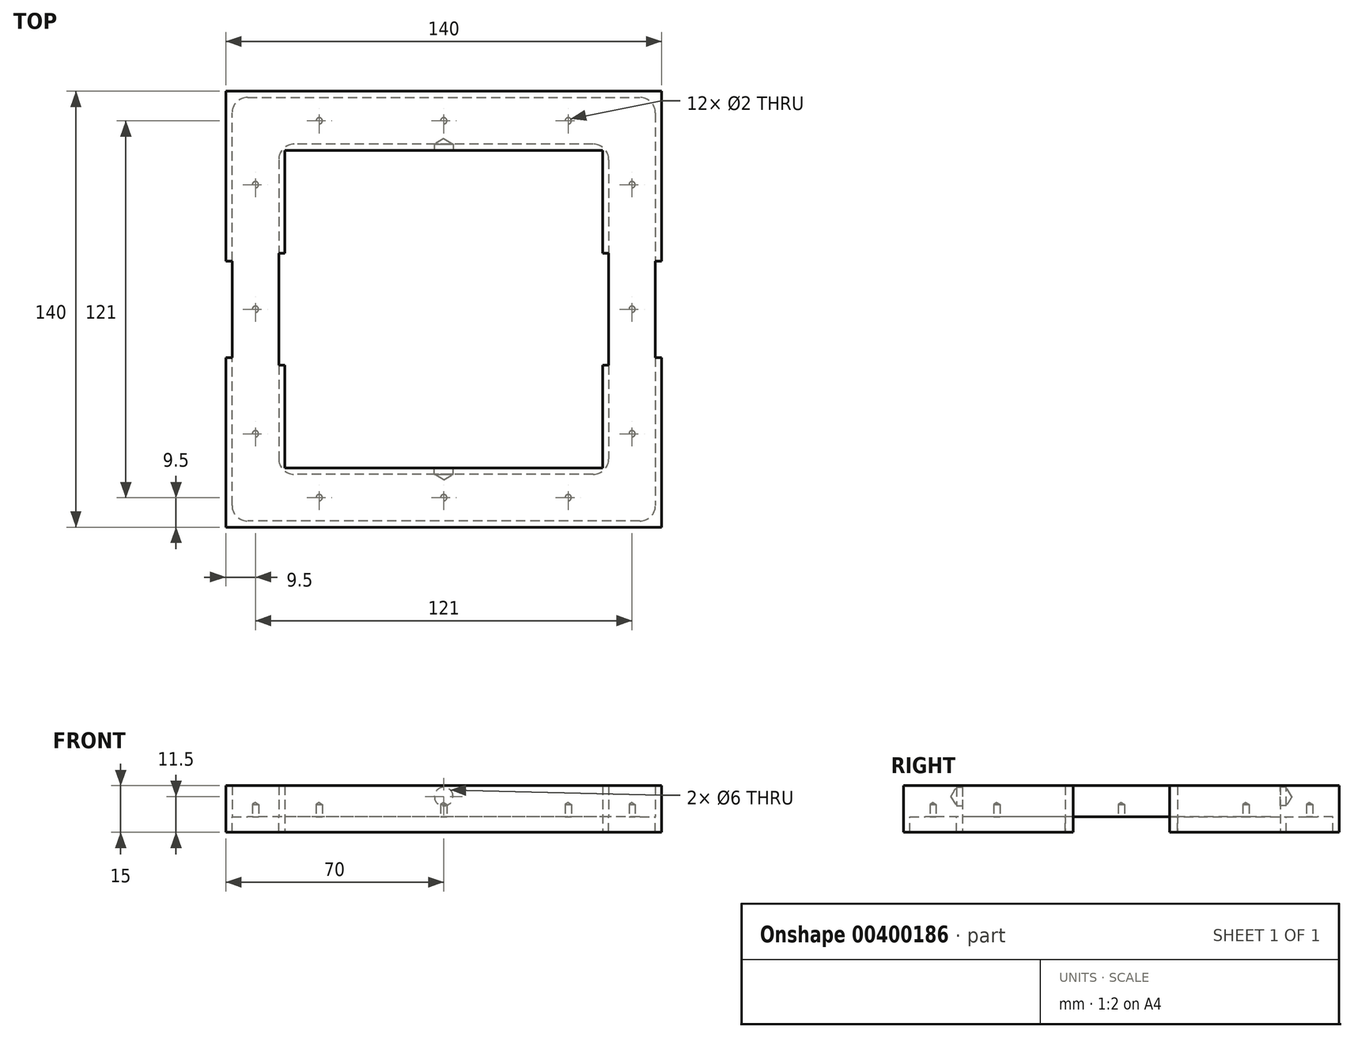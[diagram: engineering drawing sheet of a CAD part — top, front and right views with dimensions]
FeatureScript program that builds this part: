
annotation { "Feature Type Name" : "Feature", "Feature Type Description" : "" }
export const myFeature = defineFeature(function(context is Context, id is Id, definition is map)
    precondition{}
    {
        {
            var Q0;
            Q0=qCreatedBy(makeId("Top.planeOp"),FACE);
            var sketch = newSketch(context, id + "F0", { "sketchPlane" : qUnion([Q0])});
            skLineSegment(sketch, "E0.bottom", {"start": v(-70, 70) * mm, "end": v(70, 70) * mm});
            skLineSegment(sketch, "E0.top", {"start": v(-70, -70) * mm, "end": v(70, -70) * mm});
            skLineSegment(sketch, "E0.left", {"start": v(-70, 70) * mm, "end": v(-70, -70) * mm});
            skLineSegment(sketch, "E0.right", {"start": v(70, 70) * mm, "end": v(70, -70) * mm});
            skPoint(sketch, "E0.middle", {"position": v(0, 0) * mm});
            skLineSegment(sketch, "E1", {"start": v(68, 68) * mm, "end": v(68, -68) * mm});
            skLineSegment(sketch, "E2", {"start": v(68, -68) * mm, "end": v(-68, -68) * mm});
            skLineSegment(sketch, "E3", {"start": v(-68, -68) * mm, "end": v(-68, 68) * mm});
            skLineSegment(sketch, "E4", {"start": v(-68, 68) * mm, "end": v(68, 68) * mm});
            skLineSegment(sketch, "E5", {"start": v(53, -53) * mm, "end": v(-53, -53) * mm});
            skLineSegment(sketch, "E6", {"start": v(51, -51) * mm, "end": v(-51, -51) * mm});
            skLineSegment(sketch, "E7", {"start": v(-51, 51) * mm, "end": v(51, 51) * mm});
            skLineSegment(sketch, "E8", {"start": v(53, 53) * mm, "end": v(-53, 53) * mm});
            skLineSegment(sketch, "E9", {"start": v(-53, 53) * mm, "end": v(-53, -53) * mm});
            skLineSegment(sketch, "E10", {"start": v(-51, 51) * mm, "end": v(-51, -51) * mm});
            skLineSegment(sketch, "E11", {"start": v(-51, 0) * mm, "end": v(-51, 18) * mm});
            skLineSegment(sketch, "E12", {"start": v(-51, 18) * mm, "end": v(-53, 18) * mm});
            skLineSegment(sketch, "E13", {"start": v(-53, 18) * mm, "end": v(-53, -18) * mm});
            skLineSegment(sketch, "E14", {"start": v(-53, -18) * mm, "end": v(-51, -18) * mm});
            skLineSegment(sketch, "E15", {"start": v(-51, -18) * mm, "end": v(-51, 0) * mm});
            skLineSegment(sketch, "E16", {"start": v(51, 51) * mm, "end": v(51, -51) * mm});
            skLineSegment(sketch, "E17", {"start": v(53, 53) * mm, "end": v(53, -53) * mm});
            skLineSegment(sketch, "E18", {"start": v(53, 0) * mm, "end": v(53, 18) * mm});
            skLineSegment(sketch, "E19", {"start": v(53, 18) * mm, "end": v(51, 18) * mm});
            skLineSegment(sketch, "E20", {"start": v(53, 0) * mm, "end": v(53, -18) * mm});
            skLineSegment(sketch, "E21", {"start": v(53, -18) * mm, "end": v(51, -18) * mm});
            skLineSegment(sketch, "E22", {"start": v(68, 0) * mm, "end": v(68, 15.5) * mm});
            skLineSegment(sketch, "E23", {"start": v(68, 15.5) * mm, "end": v(70, 15.5) * mm});
            skLineSegment(sketch, "E24", {"start": v(68, 0) * mm, "end": v(68, -15.5) * mm});
            skLineSegment(sketch, "E25", {"start": v(68, -15.5) * mm, "end": v(70, -15.5) * mm});
            skLineSegment(sketch, "E26", {"start": v(-68, 0) * mm, "end": v(-68, 15.5) * mm});
            skLineSegment(sketch, "E27", {"start": v(-68, 15.5) * mm, "end": v(-70, 15.5) * mm});
            skLineSegment(sketch, "E28", {"start": v(-68, 0) * mm, "end": v(-68, -15.5) * mm});
            skLineSegment(sketch, "E29", {"start": v(-68, -15.5) * mm, "end": v(-70, -15.5) * mm});
            skPoint(sketch, "E30", {"position": v(0, -60.5) * mm});
            skPoint(sketch, "E31", {"position": v(60.5, 0) * mm});
            skPoint(sketch, "E32", {"position": v(0, 60.5) * mm});
            skPoint(sketch, "E33", {"position": v(-60.5, 0) * mm});
            skPoint(sketch, "E34", {"position": v(-40, -60.5) * mm});
            skPoint(sketch, "E35", {"position": v(40, -60.5) * mm});
            skPoint(sketch, "E36", {"position": v(-40, 60.5) * mm});
            skPoint(sketch, "E37", {"position": v(40, 60.5) * mm});
            skPoint(sketch, "E38", {"position": v(-60.5, -40) * mm});
            skPoint(sketch, "E39", {"position": v(-60.5, 40) * mm});
            skPoint(sketch, "E40", {"position": v(60.5, -40) * mm});
            skPoint(sketch, "E41", {"position": v(60.5, 40) * mm});
            skSolve(sketch);
        }
        {
            var Q0;
            Q0=makeQuery(id+"F0.imprint","IMPRINT",FACE,{"disambiguationData":[TD([[makeQuery(id+"F0.imprint","IMPRINT",EDGE,{"derivedFrom":sQuery(id+"F0.wireOp",EDGE,"E0.bottom")}),-1.0]])]});
            var Q1;
            Q1=makeQuery(id+"F0.imprint","IMPRINT",FACE,{"disambiguationData":[TD([[makeQuery(id+"F0.imprint","IMPRINT",EDGE,{"derivedFrom":sQuery(id+"F0.wireOp",EDGE,"E1")}),-1.0]])]});
            var Q2;
            Q2=makeQuery(id+"F0.imprint","IMPRINT",FACE,{"disambiguationData":[TD([[makeQuery(id+"F0.imprint","IMPRINT",EDGE,{"derivedFrom":sQuery(id+"F0.wireOp",EDGE,"Wn8sRztM-9DSE-PQQb-c3jE-AxI3LFL1xT7E")}),-1.0]])]});
            var Q3;
            Q3=makeQuery(id+"F0.imprint","IMPRINT",FACE,{"disambiguationData":[TD([[makeQuery(id+"F0.imprint","IMPRINT",EDGE,{"derivedFrom":sQuery(id+"F0.wireOp",EDGE,"heY1r5AS-22mk-dWtd-xOAW-OfOOxzFGAM1P")}),-1.0]])]});
            var Q4;
            {var subQ4=sQuery(id+"F0.wireOp",EDGE,"0ZnLiHHq-RTrH-7G8n-jalu-C7bSdwdgHh1i");Q4=makeQuery(id+"F0.imprint","IMPRINT",FACE,{"disambiguationData":[TD([[makeQuery(id+"F0.imprint","IMPRINT",EDGE,{"derivedFrom":subQ4}),1.0]])]});}
            var Q5;
            Q5=makeQuery(id+"F0.imprint","IMPRINT",FACE,{"disambiguationData":[TD([[makeQuery(id+"F0.imprint","IMPRINT",EDGE,{"derivedFrom":sQuery(id+"F0.wireOp",EDGE,"E26")}),1.0]])]});
            var Q6;
            {var subQ1=sQuery(id+"F0.wireOp",EDGE,"E0.top");Q6=makeQuery(id+"F0.imprint","IMPRINT",FACE,{"disambiguationData":[TD([[makeQuery(id+"F0.imprint","IMPRINT",EDGE,{"derivedFrom":subQ1}),1.0]])]});}
            var Q7;
            Q7=makeQuery(id+"F0.imprint","IMPRINT",FACE,{"disambiguationData":[TD([[makeQuery(id+"F0.imprint","IMPRINT",EDGE,{"derivedFrom":sQuery(id+"F0.wireOp",EDGE,"E22")}),-1.0]])]});
            var Q8;
            {var subQ1=sQuery(id+"F0.wireOp",EDGE,"E7");Q8=makeQuery(id+"F0.imprint","IMPRINT",FACE,{"disambiguationData":[TD([[makeQuery(id+"F0.imprint","IMPRINT",EDGE,{"derivedFrom":subQ1}),1.0]])]});}
            var Q9;
            Q9=makeQuery(id+"F0.imprint","IMPRINT",FACE,{"disambiguationData":[TD([[makeQuery(id+"F0.imprint","IMPRINT",EDGE,{"derivedFrom":sQuery(id+"F0.wireOp",EDGE,"E11")}),1.0]])]});
            var Q10;
            Q10=makeQuery(id+"F0.imprint","IMPRINT",FACE,{"disambiguationData":[TD([[makeQuery(id+"F0.imprint","IMPRINT",EDGE,{"derivedFrom":sQuery(id+"F0.wireOp",EDGE,"E18")}),1.0]])]});
            var Q11;
            {var subQ4=sQuery(id+"F0.wireOp",EDGE,"E5");Q11=makeQuery(id+"F0.imprint","IMPRINT",FACE,{"disambiguationData":[TD([[makeQuery(id+"F0.imprint","IMPRINT",EDGE,{"derivedFrom":subQ4}),-1.0]])]});}
            extrude(context, id + "F1", {"entities" : qUnion([Q0, Q1, Q2, Q3, Q4, Q5, Q6, Q7, Q8, Q9, Q10, Q11]), "depth" : 10 * mm});
        }
        {
            var Q0;
            Q0=makeQuery(id+"F0.imprint","IMPRINT",FACE,{"disambiguationData":[TD([[makeQuery(id+"F0.imprint","IMPRINT",EDGE,{"derivedFrom":sQuery(id+"F0.wireOp",EDGE,"E0.bottom")}),-1.0]])]});
            var Q1;
            Q1=makeQuery(id+"F0.imprint","IMPRINT",FACE,{"disambiguationData":[TD([[makeQuery(id+"F0.imprint","IMPRINT",EDGE,{"derivedFrom":sQuery(id+"F0.wireOp",EDGE,"Wn8sRztM-9DSE-PQQb-c3jE-AxI3LFL1xT7E")}),-1.0]])]});
            var Q2;
            {var subQ1=sQuery(id+"F0.wireOp",EDGE,"E0.top");Q2=makeQuery(id+"F0.imprint","IMPRINT",FACE,{"disambiguationData":[TD([[makeQuery(id+"F0.imprint","IMPRINT",EDGE,{"derivedFrom":subQ1}),1.0]])]});}
            var Q3;
            {var subQ4=sQuery(id+"F0.wireOp",EDGE,"E5");Q3=makeQuery(id+"F0.imprint","IMPRINT",FACE,{"disambiguationData":[TD([[makeQuery(id+"F0.imprint","IMPRINT",EDGE,{"derivedFrom":subQ4}),-1.0]])]});}
            var Q4;
            {var subQ1=sQuery(id+"F0.wireOp",EDGE,"E7");Q4=makeQuery(id+"F0.imprint","IMPRINT",FACE,{"disambiguationData":[TD([[makeQuery(id+"F0.imprint","IMPRINT",EDGE,{"derivedFrom":subQ1}),1.0]])]});}
            extrude(context, id + "F2", {"entities" : qUnion([Q0, Q1, Q2, Q3, Q4]), "operationType" : NewBodyOperationType.ADD, "oppositeDirection" : true, "depth" : 5 * mm});
        }
        {
            var Q0;
            Q0=sQuery(id+"F0.wireOp",VERTEX,"6b741a85-5c8c-4f44-8248-58c756bbbfca");
            var Q1;
            Q1=sQuery(id+"F0.wireOp",VERTEX,"E30");
            var Q2;
            Q2=sQuery(id+"F0.wireOp",VERTEX,"30763c46-4e67-4485-9359-a76c1e7a9025");
            var Q3;
            Q3=sQuery(id+"F0.wireOp",VERTEX,"6d4f6b0a-0079-43d5-8c28-538648c8d0f5");
            var Q4;
            Q4=sQuery(id+"F0.wireOp",VERTEX,"E31");
            var Q5;
            Q5=sQuery(id+"F0.wireOp",VERTEX,"4c6b8f36-78a3-45b5-8b2e-6f7322aba786");
            var Q6;
            Q6=sQuery(id+"F0.wireOp",VERTEX,"8713927f-972c-453f-9c66-a7a60fbf4d67");
            var Q7;
            Q7=sQuery(id+"F0.wireOp",VERTEX,"E32");
            var Q8;
            Q8=sQuery(id+"F0.wireOp",VERTEX,"1defa935-9a37-4483-8ab3-138fc0cdace9");
            var Q9;
            Q9=sQuery(id+"F0.wireOp",VERTEX,"1ced1939-7057-40a5-9a17-9a71a5e9f090");
            var Q10;
            Q10=sQuery(id+"F0.wireOp",VERTEX,"E33");
            var Q11;
            Q11=sQuery(id+"F0.wireOp",VERTEX,"de10a42f-2d62-4ead-983f-996f2c1775ed");
            var Q12;
            Q12=sQuery(id+"F0.wireOp",VERTEX,"E38");
            var Q13;
            Q13=sQuery(id+"F0.wireOp",VERTEX,"E34");
            var Q14;
            Q14=sQuery(id+"F0.wireOp",VERTEX,"E35");
            var Q15;
            Q15=sQuery(id+"F0.wireOp",VERTEX,"E40");
            var Q16;
            Q16=sQuery(id+"F0.wireOp",VERTEX,"E41");
            var Q17;
            Q17=sQuery(id+"F0.wireOp",VERTEX,"E37");
            var Q18;
            Q18=sQuery(id+"F0.wireOp",VERTEX,"E36");
            var Q19;
            Q19=sQuery(id+"F0.wireOp",VERTEX,"E39");
            var Q20;
            Q20=makeQuery(id+"F1.opExtrude","SWEPT_BODY",BODY,{"disambiguationData":[OSD([sQuery(id+"F0.wireOp",EDGE,"E0.bottom"),sQuery(id+"F0.wireOp",EDGE,"E0.top"),sQuery(id+"F0.wireOp",EDGE,"E0.left"),sQuery(id+"F0.wireOp",EDGE,"E0.right"),sQuery(id+"F0.wireOp",EDGE,"E6"),sQuery(id+"F0.wireOp",EDGE,"E7"),sQuery(id+"F0.wireOp",EDGE,"E10"),sQuery(id+"F0.wireOp",EDGE,"E11"),sQuery(id+"F0.wireOp",EDGE,"E15"),sQuery(id+"F0.wireOp",EDGE,"E16")])]});
            hole(context, id + "F3", {"style" : HoleStyle.SIMPLE, "endStyle" : HoleEndStyle.BLIND, "oppositeDirection" : true, "holeDiameter" : 2 * mm, "holeDepth" : 4 * mm, "isTappedThrough" : true, "tappedDepth" : 12 * mm, "tapClearance" : 3, "locations" : qUnion([Q0, Q1, Q2, Q3, Q4, Q5, Q6, Q7, Q8, Q9, Q10, Q11, Q12, Q13, Q14, Q15, Q16, Q17, Q18, Q19]), "scope" : qUnion([Q20])});
        }
        {
            var Q0;
            Q0=makeQuery(id+"F2.opExtrude","SWEPT_EDGE",EDGE,{"disambiguationData":[OSD([sQuery(id+"F0.wireOp",EDGE,"E2"),sQuery(id+"F0.wireOp",EDGE,"E3")])]});
            var Q1;
            Q1=makeQuery(id+"F2.opExtrude","SWEPT_EDGE",EDGE,{"disambiguationData":[OSD([sQuery(id+"F0.wireOp",EDGE,"E5"),sQuery(id+"F0.wireOp",EDGE,"E9")])]});
            var Q2;
            Q2=makeQuery(id+"F2.opExtrude","SWEPT_EDGE",EDGE,{"disambiguationData":[OSD([sQuery(id+"F0.wireOp",EDGE,"E8"),sQuery(id+"F0.wireOp",EDGE,"E9")])]});
            var Q3;
            Q3=makeQuery(id+"F2.opExtrude","SWEPT_EDGE",EDGE,{"disambiguationData":[OSD([sQuery(id+"F0.wireOp",EDGE,"E8"),sQuery(id+"F0.wireOp",EDGE,"E17")])]});
            var Q4;
            Q4=makeQuery(id+"F2.opExtrude","SWEPT_EDGE",EDGE,{"disambiguationData":[OSD([sQuery(id+"F0.wireOp",EDGE,"E5"),sQuery(id+"F0.wireOp",EDGE,"E17")])]});
            var Q5;
            Q5=makeQuery(id+"F2.opExtrude","SWEPT_EDGE",EDGE,{"disambiguationData":[OSD([sQuery(id+"F0.wireOp",EDGE,"E1"),sQuery(id+"F0.wireOp",EDGE,"E4")])]});
            var Q6;
            Q6=makeQuery(id+"F2.opExtrude","SWEPT_EDGE",EDGE,{"disambiguationData":[OSD([sQuery(id+"F0.wireOp",EDGE,"E3"),sQuery(id+"F0.wireOp",EDGE,"E4")])]});
            var Q7;
            Q7=makeQuery(id+"F2.opExtrude","SWEPT_EDGE",EDGE,{"disambiguationData":[OSD([sQuery(id+"F0.wireOp",EDGE,"E1"),sQuery(id+"F0.wireOp",EDGE,"E2")])]});
            fillet(context, id + "F4", {"entities" : qUnion([Q0, Q1, Q2, Q3, Q4, Q5, Q6, Q7]), "radius" : 5 * mm, "tangentPropagation" : true, "allowEdgeOverflow" : false});
        }
        {
            var Q0;
            {var subQ0=sQuery(id+"F0.wireOp",EDGE,"E7");Q0=makeQuery(id+"F2.boolean.opBoolean","MERGE",FACE,{"derivedFrom":[makeQuery(id+"F1.opExtrude","SWEPT_FACE",FACE,{"disambiguationData":[OSD([subQ0])]}),makeQuery(id+"F2.opExtrude","SWEPT_FACE",FACE,{"disambiguationData":[OSD([subQ0])]})]});}
            var sketch = newSketch(context, id + "F5", { "sketchPlane" : qUnion([Q0])});
            skPoint(sketch, "E42", {"position": v(0, 6.5) * mm});
            skSolve(sketch);
        }
        {
            var Q0;
            Q0=sQuery(id+"F5.wireOp",VERTEX,"E42");
            var Q1;
            Q1=makeQuery(id+"F1.opExtrude","SWEPT_BODY",BODY,{"disambiguationData":[OSD([sQuery(id+"F0.wireOp",EDGE,"E0.bottom"),sQuery(id+"F0.wireOp",EDGE,"E0.top"),sQuery(id+"F0.wireOp",EDGE,"E0.left"),sQuery(id+"F0.wireOp",EDGE,"E0.right"),sQuery(id+"F0.wireOp",EDGE,"E6"),sQuery(id+"F0.wireOp",EDGE,"E7"),sQuery(id+"F0.wireOp",EDGE,"E10"),sQuery(id+"F0.wireOp",EDGE,"E11"),sQuery(id+"F0.wireOp",EDGE,"E15"),sQuery(id+"F0.wireOp",EDGE,"E16")])]});
            hole(context, id + "F6", {"style" : HoleStyle.SIMPLE, "endStyle" : HoleEndStyle.BLIND, "holeDiameter" : 6 * mm, "holeDepth" : 2 * mm, "isTappedThrough" : true, "tappedDepth" : 12 * mm, "tapClearance" : 3, "startFromSketch" : true, "locations" : qUnion([Q0]), "scope" : qUnion([Q1])});
        }
        {
            var Q0;
            {var subQ0=sQuery(id+"F0.wireOp",EDGE,"E6");Q0=makeQuery(id+"F2.boolean.opBoolean","MERGE",FACE,{"derivedFrom":[makeQuery(id+"F1.opExtrude","SWEPT_FACE",FACE,{"disambiguationData":[OSD([subQ0])]}),makeQuery(id+"F2.opExtrude","SWEPT_FACE",FACE,{"disambiguationData":[OSD([subQ0])]})]});}
            var sketch = newSketch(context, id + "F7", { "sketchPlane" : qUnion([Q0])});
            skPoint(sketch, "E43", {"position": v(0, 6.5) * mm});
            skSolve(sketch);
        }
        {
            var Q0;
            Q0=sQuery(id+"F7.wireOp",VERTEX,"E43");
            var Q1;
            Q1=makeQuery(id+"F1.opExtrude","SWEPT_BODY",BODY,{"disambiguationData":[OSD([sQuery(id+"F0.wireOp",EDGE,"E0.bottom"),sQuery(id+"F0.wireOp",EDGE,"E0.top"),sQuery(id+"F0.wireOp",EDGE,"E0.left"),sQuery(id+"F0.wireOp",EDGE,"E0.right"),sQuery(id+"F0.wireOp",EDGE,"E6"),sQuery(id+"F0.wireOp",EDGE,"E7"),sQuery(id+"F0.wireOp",EDGE,"E10"),sQuery(id+"F0.wireOp",EDGE,"E11"),sQuery(id+"F0.wireOp",EDGE,"E15"),sQuery(id+"F0.wireOp",EDGE,"E16")])]});
            hole(context, id + "F8", {"style" : HoleStyle.SIMPLE, "endStyle" : HoleEndStyle.BLIND, "holeDiameter" : 6 * mm, "holeDepth" : 2 * mm, "isTappedThrough" : true, "tappedDepth" : 12 * mm, "tapClearance" : 3, "startFromSketch" : true, "locations" : qUnion([Q0]), "scope" : qUnion([Q1])});
        }
    });
